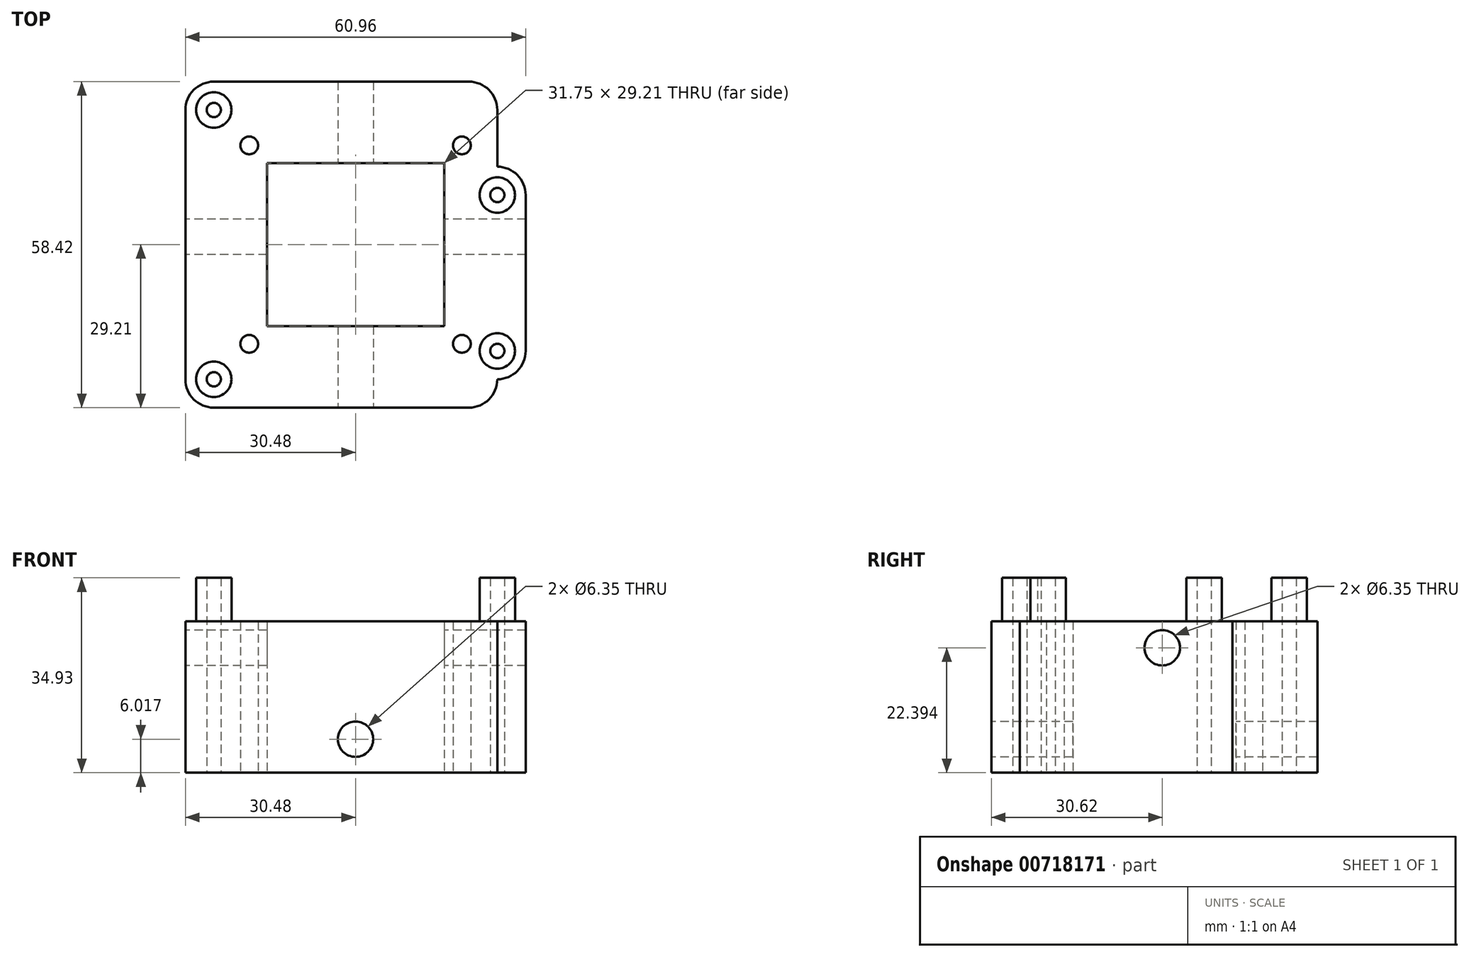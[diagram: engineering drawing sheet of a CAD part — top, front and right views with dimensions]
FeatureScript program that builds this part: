
annotation { "Feature Type Name" : "Feature", "Feature Type Description" : "" }
export const myFeature = defineFeature(function(context is Context, id is Id, definition is map)
    precondition{}
    {
        {
            var Q0;
            Q0=qCreatedBy(makeId("Top.planeOp"),FACE);
            var sketch = newSketch(context, id + "F0", { "sketchPlane" : qUnion([Q0])});
            skLineSegment(sketch, "E0.bottom", {"start": v(31.75, -30.48) * mm, "end": v(-31.75, -30.48) * mm});
            skLineSegment(sketch, "E0.top", {"start": v(31.75, 30.48) * mm, "end": v(-31.75, 30.48) * mm});
            skLineSegment(sketch, "E0.left", {"start": v(31.75, -30.48) * mm, "end": v(31.75, 30.48) * mm});
            skLineSegment(sketch, "E0.right", {"start": v(-31.75, -30.48) * mm, "end": v(-31.75, 30.48) * mm});
            skPoint(sketch, "E0.middle", {"position": v(0, 0) * mm});
            skLineSegment(sketch, "E1.bottom", {"start": v(25.4, -24.13) * mm, "end": v(-25.4, -24.13) * mm});
            skLineSegment(sketch, "E1.top", {"start": v(25.4, 24.13) * mm, "end": v(-25.4, 24.13) * mm});
            skLineSegment(sketch, "E1.left", {"start": v(25.4, -24.13) * mm, "end": v(25.4, 24.13) * mm});
            skLineSegment(sketch, "E1.right", {"start": v(-25.4, -24.13) * mm, "end": v(-25.4, 24.13) * mm});
            skLineSegment(sketch, "E2", {"start": v(-25.4, 8.9) * mm, "end": v(25.4, 8.9) * mm});
            skLineSegment(sketch, "E3", {"start": v(-25.4, -19.05) * mm, "end": v(25.4, -19.05) * mm});
            skLineSegment(sketch, "E4.bottom", {"start": v(19.05, -17.78) * mm, "end": v(-19.05, -17.78) * mm});
            skLineSegment(sketch, "E4.top", {"start": v(19.05, 17.78) * mm, "end": v(-19.05, 17.78) * mm});
            skLineSegment(sketch, "E4.left", {"start": v(19.05, -17.78) * mm, "end": v(19.05, 17.78) * mm});
            skLineSegment(sketch, "E4.right", {"start": v(-19.05, -17.78) * mm, "end": v(-19.05, 17.78) * mm});
            skSolve(sketch);
        }
        {
            var Q0;
            Q0=qCreatedBy(makeId("Top.planeOp"),FACE);
            var sketch = newSketch(context, id + "F1", { "sketchPlane" : qUnion([Q0])});
            skPoint(sketch, "E5.0", {"position": v(-25.4, -24.13) * mm});
            skPoint(sketch, "E6.0", {"position": v(25.4, -19.05) * mm});
            skPoint(sketch, "E7.0", {"position": v(25.4, 8.9) * mm});
            skPoint(sketch, "E8.0", {"position": v(-25.4, 24.13) * mm});
            skPoint(sketch, "E9.middle", {"position": v(0, 0) * mm});
            skCircle(sketch, "E10", {"center": v(-25.4, 24.13) * mm, "radius": 3.18 * mm});
            skCircle(sketch, "E11", {"center": v(-25.4, -24.13) * mm, "radius": 3.18 * mm});
            skCircle(sketch, "E12", {"center": v(25.4, -19.05) * mm, "radius": 3.18 * mm});
            skCircle(sketch, "E13", {"center": v(25.4, 8.9) * mm, "radius": 3.18 * mm});
            skLineSegment(sketch, "E14.bottom", {"start": v(30.48, -29.21) * mm, "end": v(-30.48, -29.21) * mm});
            skLineSegment(sketch, "E14.top", {"start": v(30.48, 29.21) * mm, "end": v(-30.48, 29.21) * mm});
            skLineSegment(sketch, "E14.left", {"start": v(30.48, -29.21) * mm, "end": v(30.48, 29.21) * mm});
            skLineSegment(sketch, "E14.right", {"start": v(-30.48, -29.21) * mm, "end": v(-30.48, 29.21) * mm});
            skLineSegment(sketch, "E15.bottom", {"start": v(25.4, 29.21) * mm, "end": v(30.48, 29.21) * mm});
            skLineSegment(sketch, "E15.top", {"start": v(25.4, 13.97) * mm, "end": v(30.48, 13.97) * mm});
            skLineSegment(sketch, "E15.left", {"start": v(25.4, 29.21) * mm, "end": v(25.4, 13.97) * mm});
            skLineSegment(sketch, "E15.right", {"start": v(30.48, 29.21) * mm, "end": v(30.48, 13.97) * mm});
            skLineSegment(sketch, "E16.bottom", {"start": v(30.48, -29.21) * mm, "end": v(25.4, -29.21) * mm});
            skLineSegment(sketch, "E16.top", {"start": v(30.48, -24.13) * mm, "end": v(25.4, -24.13) * mm});
            skLineSegment(sketch, "E16.left", {"start": v(30.48, -29.21) * mm, "end": v(30.48, -24.13) * mm});
            skLineSegment(sketch, "E16.right", {"start": v(25.4, -29.21) * mm, "end": v(25.4, -24.13) * mm});
            skPoint(sketch, "E17.0", {"position": v(19.05, -17.78) * mm});
            skPoint(sketch, "E18.0", {"position": v(19.05, 17.78) * mm});
            skPoint(sketch, "E19.0", {"position": v(-19.05, -17.78) * mm});
            skPoint(sketch, "E20.0", {"position": v(-19.05, 17.78) * mm});
            skCircle(sketch, "E21", {"center": v(-25.4, 24.13) * mm, "radius": 1.27 * mm});
            skCircle(sketch, "E22", {"center": v(25.4, 8.9) * mm, "radius": 1.27 * mm});
            skCircle(sketch, "E23", {"center": v(25.4, -19.05) * mm, "radius": 1.27 * mm});
            skCircle(sketch, "E24", {"center": v(-25.4, -24.13) * mm, "radius": 1.27 * mm});
            skCircle(sketch, "E25", {"center": v(-19.05, -17.78) * mm, "radius": 1.59 * mm});
            skCircle(sketch, "E26", {"center": v(-19.05, 17.78) * mm, "radius": 1.59 * mm});
            skCircle(sketch, "E27", {"center": v(19.05, 17.78) * mm, "radius": 1.59 * mm});
            skCircle(sketch, "E28", {"center": v(19.05, -17.78) * mm, "radius": 1.59 * mm});
            skLineSegment(sketch, "E29.bottom", {"start": v(15.88, -14.6) * mm, "end": v(-15.88, -14.6) * mm});
            skLineSegment(sketch, "E29.top", {"start": v(15.88, 14.6) * mm, "end": v(-15.88, 14.6) * mm});
            skLineSegment(sketch, "E29.left", {"start": v(15.88, -14.6) * mm, "end": v(15.87, 14.6) * mm});
            skLineSegment(sketch, "E29.right", {"start": v(-15.87, -14.6) * mm, "end": v(-15.88, 14.6) * mm});
            skSolve(sketch);
        }
        {
            var Q0;
            Q0=makeQuery(id+"F1.imprint","IMPRINT",FACE,{"disambiguationData":[TD([[makeQuery(id+"F1.imprint","IMPRINT",EDGE,{"derivedFrom":sQuery(id+"F1.wireOp",EDGE,"E10")}),-1.0]])]});
            extrude(context, id + "F2", {"entities" : qUnion([Q0]), "depth" : 1.71 * mm});
        }
        {
            var Q0;
            Q0=makeQuery(id+"F1.imprint","IMPRINT",FACE,{"disambiguationData":[TD([[makeQuery(id+"F1.imprint","IMPRINT",EDGE,{"derivedFrom":sQuery(id+"F1.wireOp",EDGE,"E11")}),1.0]])]});
            var Q1;
            Q1=makeQuery(id+"F1.imprint","IMPRINT",FACE,{"disambiguationData":[TD([[makeQuery(id+"F1.imprint","IMPRINT",EDGE,{"derivedFrom":sQuery(id+"F1.wireOp",EDGE,"E12")}),1.0]])]});
            var Q2;
            Q2=makeQuery(id+"F1.imprint","IMPRINT",FACE,{"disambiguationData":[TD([[makeQuery(id+"F1.imprint","IMPRINT",EDGE,{"derivedFrom":sQuery(id+"F1.wireOp",EDGE,"E13")}),1.0]])]});
            var Q3;
            Q3=makeQuery(id+"F1.imprint","IMPRINT",FACE,{"disambiguationData":[TD([[makeQuery(id+"F1.imprint","IMPRINT",EDGE,{"derivedFrom":sQuery(id+"F1.wireOp",EDGE,"E10")}),1.0]])]});
            extrude(context, id + "F3", {"entities" : qUnion([Q0, Q1, Q2, Q3]), "operationType" : NewBodyOperationType.ADD, "depth" : 9.52 * mm});
        }
        {
            var Q0;
            Q0=makeQuery(id+"F2.opExtrude","SWEPT_EDGE",EDGE,{"disambiguationData":[OSD([sQuery(id+"F1.wireOp",EDGE,"E14.top"),sQuery(id+"F1.wireOp",EDGE,"E15.bottom"),sQuery(id+"F1.wireOp",EDGE,"E15.left")])]});
            var Q1;
            Q1=makeQuery(id+"F2.opExtrude","SWEPT_EDGE",EDGE,{"disambiguationData":[OSD([sQuery(id+"F1.wireOp",EDGE,"E14.left"),sQuery(id+"F1.wireOp",EDGE,"E15.top"),sQuery(id+"F1.wireOp",EDGE,"E15.right")])]});
            var Q2;
            Q2=makeQuery(id+"F2.opExtrude","SWEPT_EDGE",EDGE,{"disambiguationData":[OSD([sQuery(id+"F1.wireOp",EDGE,"E14.left"),sQuery(id+"F1.wireOp",EDGE,"E16.top"),sQuery(id+"F1.wireOp",EDGE,"E16.left")])]});
            var Q3;
            Q3=makeQuery(id+"F2.opExtrude","SWEPT_EDGE",EDGE,{"disambiguationData":[OSD([sQuery(id+"F1.wireOp",EDGE,"E14.bottom"),sQuery(id+"F1.wireOp",EDGE,"E16.bottom"),sQuery(id+"F1.wireOp",EDGE,"E16.right")])]});
            var Q4;
            Q4=makeQuery(id+"F2.opExtrude","SWEPT_EDGE",EDGE,{"disambiguationData":[OSD([sQuery(id+"F1.wireOp",EDGE,"E14.bottom"),sQuery(id+"F1.wireOp",EDGE,"E14.right")])]});
            var Q5;
            Q5=makeQuery(id+"F2.opExtrude","SWEPT_EDGE",EDGE,{"disambiguationData":[OSD([sQuery(id+"F1.wireOp",EDGE,"E14.top"),sQuery(id+"F1.wireOp",EDGE,"E14.right")])]});
            fillet(context, id + "F4", {"entities" : qUnion([Q0, Q1, Q2, Q3, Q4, Q5]), "radius" : 5.08 * mm, "tangentPropagation" : true, "allowEdgeOverflow" : false});
        }
        {
            var Q0;
            {var subQ0=sQuery(id+"F1.wireOp",EDGE,"E13");var subQ1=sQuery(id+"F1.wireOp",EDGE,"E12");var subQ2=sQuery(id+"F1.wireOp",EDGE,"E11");var subQ3=sQuery(id+"F1.wireOp",EDGE,"E10");Q0=makeQuery(id+"F3.boolean.opBoolean","MERGE",FACE,{"derivedFrom":[makeQuery(id+"F2.opExtrude","CAP_FACE",FACE,{"disambiguationData":[OSD([subQ3,subQ2,subQ1,subQ0,sQuery(id+"F1.wireOp",EDGE,"E14.bottom"),sQuery(id+"F1.wireOp",EDGE,"E14.top"),sQuery(id+"F1.wireOp",EDGE,"E14.left"),sQuery(id+"F1.wireOp",EDGE,"E14.right"),sQuery(id+"F1.wireOp",EDGE,"E15.top"),sQuery(id+"F1.wireOp",EDGE,"E15.left"),sQuery(id+"F1.wireOp",EDGE,"E16.top"),sQuery(id+"F1.wireOp",EDGE,"E16.right"),sQuery(id+"F1.wireOp",EDGE,"E25"),sQuery(id+"F1.wireOp",EDGE,"E26"),sQuery(id+"F1.wireOp",EDGE,"E27"),sQuery(id+"F1.wireOp",EDGE,"E28"),sQuery(id+"F1.wireOp",EDGE,"E29.bottom"),sQuery(id+"F1.wireOp",EDGE,"E29.top"),sQuery(id+"F1.wireOp",EDGE,"E29.left"),sQuery(id+"F1.wireOp",EDGE,"E29.right")])],"isStart":true}),makeQuery(id+"F3.opExtrude","CAP_FACE",FACE,{"disambiguationData":[OSD([subQ3,sQuery(id+"F1.wireOp",EDGE,"E21")])],"isStart":true}),makeQuery(id+"F3.opExtrude","CAP_FACE",FACE,{"disambiguationData":[OSD([subQ2,sQuery(id+"F1.wireOp",EDGE,"E24")])],"isStart":true}),makeQuery(id+"F3.opExtrude","CAP_FACE",FACE,{"disambiguationData":[OSD([subQ1,sQuery(id+"F1.wireOp",EDGE,"E23")])],"isStart":true}),makeQuery(id+"F3.opExtrude","CAP_FACE",FACE,{"disambiguationData":[OSD([subQ0,sQuery(id+"F1.wireOp",EDGE,"E22")])],"isStart":true})]});}
            var sketch = newSketch(context, id + "F5", { "sketchPlane" : qUnion([Q0])});
            skSolve(sketch);
        }
        {
            var Q0;
            {var subQ19=sQuery(id+"F1.wireOp",EDGE,"E25");Q0=makeQuery(id+"F5.imprint","IMPRINT",FACE,{"disambiguationData":[TD([[makeQuery(id+"F5.imprint","IMPRINT",EDGE,{"derivedFrom":makeQuery(id+"F2.opExtrude","CAP_EDGE",EDGE,{"disambiguationData":[OSD([subQ19])],"isStart":true})}),1.0]])]});}
            extrude(context, id + "F6", {"entities" : qUnion([Q0]), "operationType" : NewBodyOperationType.ADD, "depth" : 25.4 * mm, "offsetDistance" : 25.4 * mm});
        }
        {
            var Q0;
            {var subQ0=sQuery(id+"F1.wireOp",EDGE,"E14.right");Q0=makeQuery(id+"F6.boolean.opBoolean","MERGE",FACE,{"derivedFrom":[makeQuery(id+"F2.opExtrude","SWEPT_FACE",FACE,{"disambiguationData":[OSD([subQ0])]}),makeQuery(id+"F6.opExtrude","SWEPT_FACE",FACE,{"disambiguationData":[OSD([subQ0])]})]});}
            var sketch = newSketch(context, id + "F7", { "sketchPlane" : qUnion([Q0])});
            skCircle(sketch, "E30", {"center": v(-1.4, -3) * mm, "radius": 2.73 * mm});
            skSolve(sketch);
        }
        {
            var Q0;
            Q0=sQuery(id+"F7.wireOp",VERTEX,"E30.center");
            var Q1;
            Q1=makeQuery(id+"F2.opExtrude","SWEPT_BODY",BODY,{"disambiguationData":[OSD([sQuery(id+"F1.wireOp",EDGE,"E10"),sQuery(id+"F1.wireOp",EDGE,"E11"),sQuery(id+"F1.wireOp",EDGE,"E12"),sQuery(id+"F1.wireOp",EDGE,"E13"),sQuery(id+"F1.wireOp",EDGE,"E14.bottom"),sQuery(id+"F1.wireOp",EDGE,"E14.top"),sQuery(id+"F1.wireOp",EDGE,"E14.left"),sQuery(id+"F1.wireOp",EDGE,"E14.right"),sQuery(id+"F1.wireOp",EDGE,"E15.top"),sQuery(id+"F1.wireOp",EDGE,"E15.left"),sQuery(id+"F1.wireOp",EDGE,"E16.top"),sQuery(id+"F1.wireOp",EDGE,"E16.right"),sQuery(id+"F1.wireOp",EDGE,"E25"),sQuery(id+"F1.wireOp",EDGE,"E26"),sQuery(id+"F1.wireOp",EDGE,"E27"),sQuery(id+"F1.wireOp",EDGE,"E28"),sQuery(id+"F1.wireOp",EDGE,"E29.bottom"),sQuery(id+"F1.wireOp",EDGE,"E29.top"),sQuery(id+"F1.wireOp",EDGE,"E29.left"),sQuery(id+"F1.wireOp",EDGE,"E29.right")])]});
            hole(context, id + "F8", {"style" : HoleStyle.SIMPLE, "endStyle" : HoleEndStyle.THROUGH, "holeDiameter" : 6.35 * mm, "majorDiameter" : 6.35 * mm, "isTappedThrough" : true, "tappedDepth" : 12.7 * mm, "tapClearance" : 3, "locations" : qUnion([Q0]), "scope" : qUnion([Q1])});
        }
        {
            var Q0;
            {var subQ0=sQuery(id+"F1.wireOp",EDGE,"E14.bottom");Q0=makeQuery(id+"F6.boolean.opBoolean","MERGE",FACE,{"derivedFrom":[makeQuery(id+"F2.opExtrude","SWEPT_FACE",FACE,{"disambiguationData":[OSD([subQ0])]}),makeQuery(id+"F6.opExtrude","SWEPT_FACE",FACE,{"disambiguationData":[OSD([subQ0])]})]});}
            var sketch = newSketch(context, id + "F9", { "sketchPlane" : qUnion([Q0])});
            skCircle(sketch, "E31", {"center": v(0, -19.38) * mm, "radius": 3.42 * mm});
            skSolve(sketch);
        }
        {
            var Q0;
            Q0=sQuery(id+"F9.wireOp",VERTEX,"E31.center");
            var Q1;
            Q1=makeQuery(id+"F2.opExtrude","SWEPT_BODY",BODY,{"disambiguationData":[OSD([sQuery(id+"F1.wireOp",EDGE,"E10"),sQuery(id+"F1.wireOp",EDGE,"E11"),sQuery(id+"F1.wireOp",EDGE,"E12"),sQuery(id+"F1.wireOp",EDGE,"E13"),sQuery(id+"F1.wireOp",EDGE,"E14.bottom"),sQuery(id+"F1.wireOp",EDGE,"E14.top"),sQuery(id+"F1.wireOp",EDGE,"E14.left"),sQuery(id+"F1.wireOp",EDGE,"E14.right"),sQuery(id+"F1.wireOp",EDGE,"E15.top"),sQuery(id+"F1.wireOp",EDGE,"E15.left"),sQuery(id+"F1.wireOp",EDGE,"E16.top"),sQuery(id+"F1.wireOp",EDGE,"E16.right"),sQuery(id+"F1.wireOp",EDGE,"E25"),sQuery(id+"F1.wireOp",EDGE,"E26"),sQuery(id+"F1.wireOp",EDGE,"E27"),sQuery(id+"F1.wireOp",EDGE,"E28"),sQuery(id+"F1.wireOp",EDGE,"E29.bottom"),sQuery(id+"F1.wireOp",EDGE,"E29.top"),sQuery(id+"F1.wireOp",EDGE,"E29.left"),sQuery(id+"F1.wireOp",EDGE,"E29.right")])]});
            hole(context, id + "F10", {"style" : HoleStyle.SIMPLE, "endStyle" : HoleEndStyle.THROUGH, "holeDiameter" : 6.35 * mm, "majorDiameter" : 6.35 * mm, "isTappedThrough" : true, "tappedDepth" : 12.7 * mm, "tapClearance" : 3, "locations" : qUnion([Q0]), "scope" : qUnion([Q1])});
        }
    });
